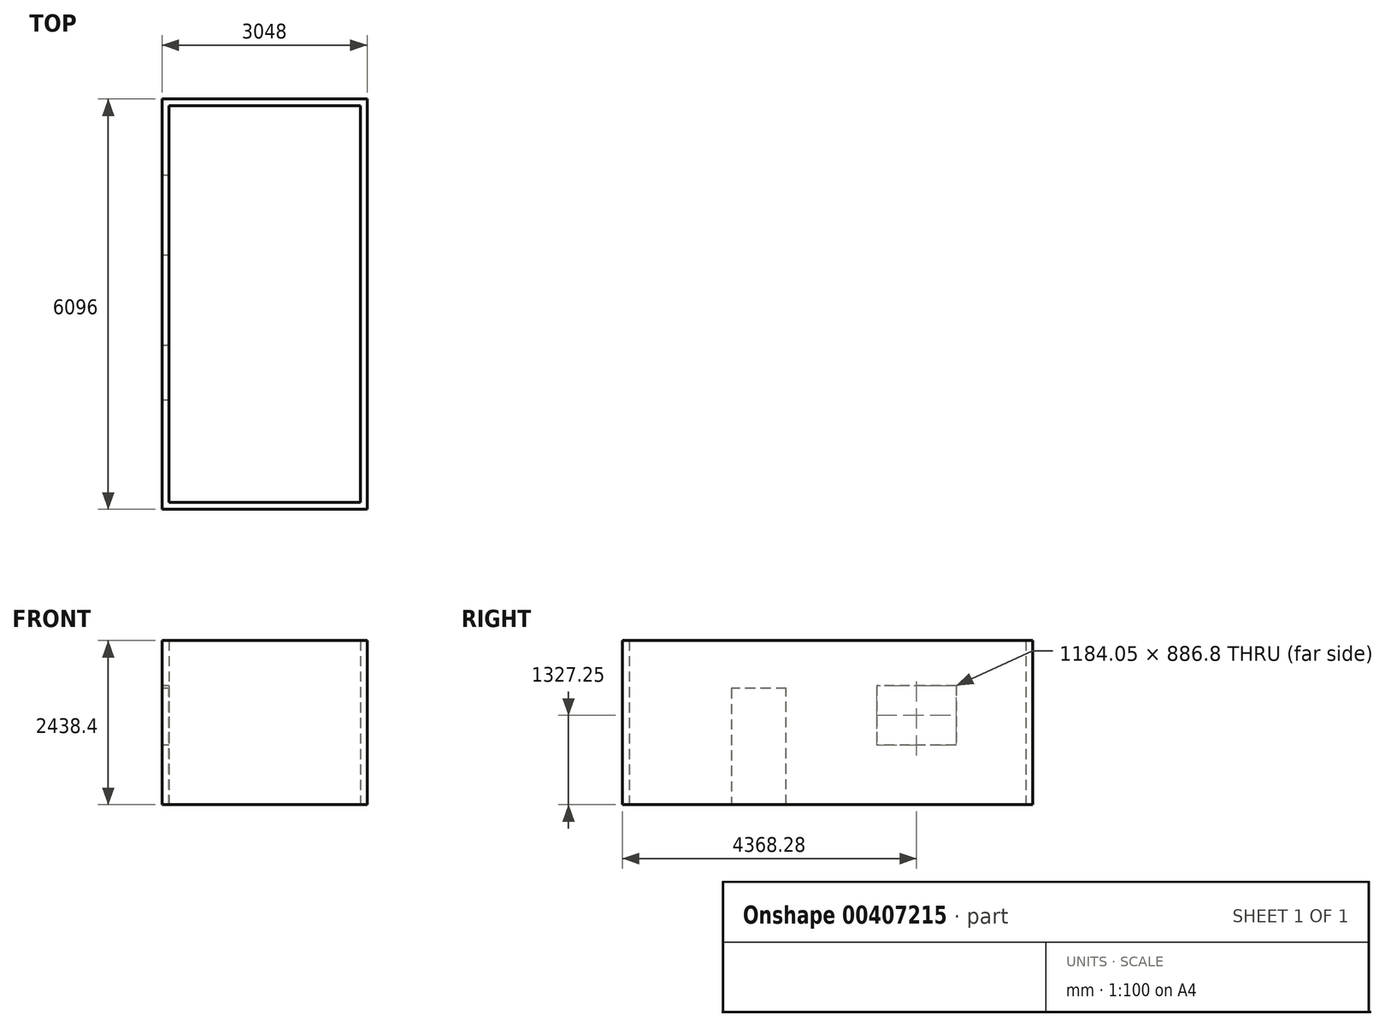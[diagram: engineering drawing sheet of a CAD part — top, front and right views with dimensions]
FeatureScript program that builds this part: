
annotation { "Feature Type Name" : "Feature", "Feature Type Description" : "" }
export const myFeature = defineFeature(function(context is Context, id is Id, definition is map)
    precondition{}
    {
        {
            var Q0;
            Q0=qCreatedBy(makeId("Top.planeOp"),FACE);
            var sketch = newSketch(context, id + "F0", { "sketchPlane" : qUnion([Q0])});
            skLineSegment(sketch, "E0.bottom", {"start": v(-999.72, 4838.6) * mm, "end": v(2048.28, 4838.6) * mm});
            skLineSegment(sketch, "E0.top", {"start": v(-999.72, -1257.4) * mm, "end": v(2048.28, -1257.4) * mm});
            skLineSegment(sketch, "E0.left", {"start": v(-999.72, 4838.6) * mm, "end": v(-999.72, -1257.4) * mm});
            skLineSegment(sketch, "E0.right", {"start": v(2048.28, 4838.6) * mm, "end": v(2048.28, -1257.4) * mm});
            skLineSegment(sketch, "E1.bottom", {"start": v(-898.12, 4737) * mm, "end": v(1946.68, 4737) * mm});
            skLineSegment(sketch, "E1.top", {"start": v(-898.12, -1155.8) * mm, "end": v(1946.68, -1155.8) * mm});
            skLineSegment(sketch, "E1.left", {"start": v(-898.12, 4737) * mm, "end": v(-898.12, -1155.8) * mm});
            skLineSegment(sketch, "E1.right", {"start": v(1946.68, 4737) * mm, "end": v(1946.68, -1155.8) * mm});
            skSolve(sketch);
        }
        {
            var Q0;
            Q0 = qSketchRegion(id + "F0", true);
            extrude(context, id + "F1", {"entities" : qUnion([Q0]), "depth" : 2438.4 * mm});
        }
        {
            var Q0;
            Q0=makeQuery(id+"F1.opExtrude","SWEPT_FACE",FACE,{"disambiguationData":[OSD([sQuery(id+"F0.wireOp",EDGE,"E0.left")])]});
            var sketch = newSketch(context, id + "F2", { "sketchPlane" : qUnion([Q0])});
            skLineSegment(sketch, "E2", {"start": v(-1176.29, 0) * mm, "end": v(-1176.29, 1727.2) * mm});
            skLineSegment(sketch, "E3", {"start": v(-1176.29, 1727.2) * mm, "end": v(-363.49, 1727.2) * mm});
            skLineSegment(sketch, "E4", {"start": v(-363.49, 1727.2) * mm, "end": v(-363.49, 0) * mm});
            skLineSegment(sketch, "E5.bottom", {"start": v(-3702.92, 1770.65) * mm, "end": v(-2518.87, 1770.65) * mm});
            skLineSegment(sketch, "E5.top", {"start": v(-3702.92, 883.85) * mm, "end": v(-2518.87, 883.85) * mm});
            skLineSegment(sketch, "E5.left", {"start": v(-3702.92, 1770.65) * mm, "end": v(-3702.92, 883.85) * mm});
            skLineSegment(sketch, "E5.right", {"start": v(-2518.87, 1770.65) * mm, "end": v(-2518.87, 883.85) * mm});
            skSolve(sketch);
        }
        {
            var Q0;
            Q0=makeQuery(id+"F2.imprint","IMPRINT",FACE,{"disambiguationData":[TD([[makeQuery(id+"F2.imprint","IMPRINT",EDGE,{"derivedFrom":sQuery(id+"F2.wireOp",EDGE,"E5.bottom")}),-1.0]])]});
            var Q1;
            {var subQ0=sQuery(id+"F2.wireOp",EDGE,"E2");Q1=makeQuery(id+"F2.imprint","IMPRINT",FACE,{"disambiguationData":[TD([[makeQuery(id+"F2.imprint","IMPRINT",EDGE,{"derivedFrom":subQ0}),-1.0]])]});}
            extrude(context, id + "F3", {"entities" : qUnion([Q0, Q1]), "operationType" : NewBodyOperationType.REMOVE, "endBound" : BoundingType.UP_TO_NEXT, "oppositeDirection" : true, "depth" : 25.4 * mm});
        }
    });
